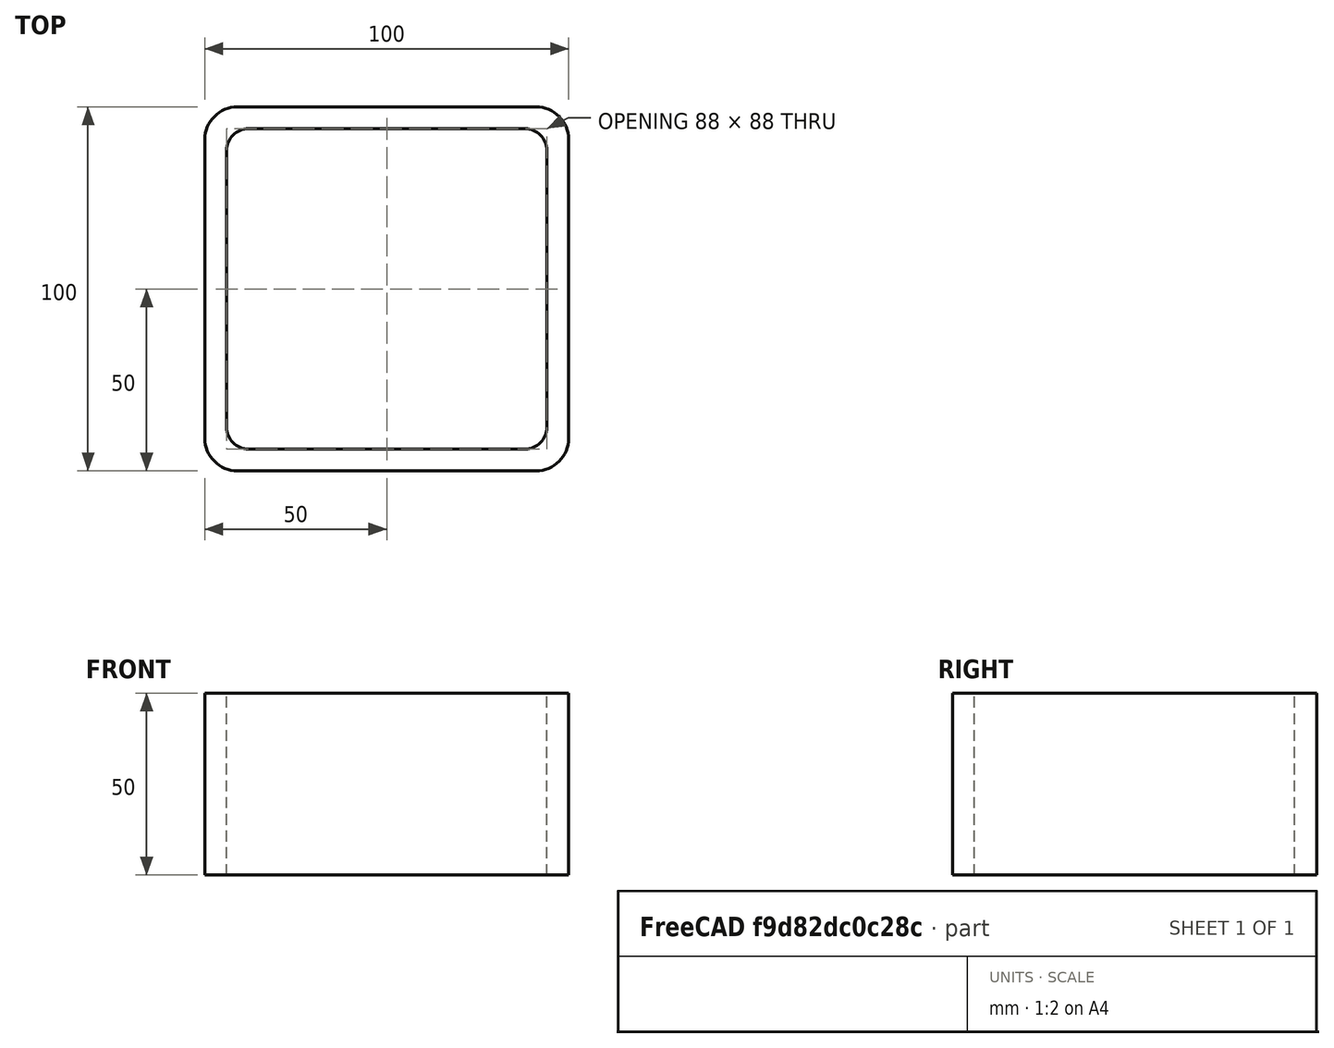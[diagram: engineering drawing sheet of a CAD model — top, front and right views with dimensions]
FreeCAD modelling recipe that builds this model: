
FCSTD DOCUMENT  (FreeCAD 0.15R4671 (Git))
Label: Square hollow section 100x100x6 EN10219 S235JRH
License: All rights reserved
LicenseURL: http://en.wikipedia.org/wiki/All_rights_reserved
objects: Sketcher::SketchObject×1, Part::Extrusion×1
note: 2 computed .brp shape members not serialized (recipe doc carries the construction recipe); baked Part::Feature solids carry a one-line shape summary decoded from their .brp

FEATURE [Sketcher::SketchObject] Sketch
  sketch-geometry (16):
    g0: LineSegment StartX=-38 StartY=44 StartZ=0 EndX=38 EndY=44 EndZ=0
    g1: LineSegment StartX=44 StartY=38 StartZ=0 EndX=44 EndY=-38 EndZ=0
    g2: LineSegment StartX=38 StartY=-44 StartZ=0 EndX=-38 EndY=-44 EndZ=0
    g3: LineSegment StartX=-44 StartY=-38 StartZ=0 EndX=-44 EndY=38 EndZ=0
    g4: LineSegment StartX=-41 StartY=50 StartZ=0 EndX=41 EndY=50 EndZ=0
    g5: LineSegment StartX=50 StartY=41 StartZ=0 EndX=50 EndY=-41 EndZ=0
    g6: LineSegment StartX=41 StartY=-50 StartZ=0 EndX=-41 EndY=-50 EndZ=0
    g7: LineSegment StartX=-50 StartY=-41 StartZ=0 EndX=-50 EndY=41 EndZ=0
    g8: ArcOfCircle CenterX=-38 CenterY=38 CenterZ=0 NormalX=0 NormalY=0 NormalZ=1 Radius=6 StartAngle=1.5708 EndAngle=3.14159
    g9: ArcOfCircle CenterX=38 CenterY=38 CenterZ=0 NormalX=0 NormalY=0 NormalZ=1 Radius=6 StartAngle=0 EndAngle=1.5708
    g10: ArcOfCircle CenterX=38 CenterY=-38 CenterZ=0 NormalX=0 NormalY=0 NormalZ=1 Radius=6 StartAngle=4.71239 EndAngle=6.28319
    g11: ArcOfCircle CenterX=-38 CenterY=-38 CenterZ=0 NormalX=0 NormalY=0 NormalZ=1 Radius=6 StartAngle=3.14159 EndAngle=4.71239
    g12: ArcOfCircle CenterX=41 CenterY=41 CenterZ=0 NormalX=0 NormalY=0 NormalZ=1 Radius=9 StartAngle=0 EndAngle=1.5708
    g13: ArcOfCircle CenterX=41 CenterY=-41 CenterZ=0 NormalX=0 NormalY=0 NormalZ=1 Radius=9 StartAngle=4.71239 EndAngle=6.28319
    g14: ArcOfCircle CenterX=-41 CenterY=-41 CenterZ=0 NormalX=0 NormalY=0 NormalZ=1 Radius=9 StartAngle=3.14159 EndAngle=4.71239
    g15: ArcOfCircle CenterX=-41 CenterY=41 CenterZ=0 NormalX=0 NormalY=0 NormalZ=1 Radius=9 StartAngle=1.5708 EndAngle=3.14159
  constraints (36):
    c: Horizontal(g2)
    c: Vertical(g3)
    c: Horizontal(g6)
    c: Vertical(g7)
    c: Tangent(g3,g8) = 1.5708
    c: Tangent(g0,g8) = 1.5708
    c: Tangent(g0,g9) = 1.5708
    c: Tangent(g1,g9) = 1.5708
    c: Tangent(g1,g10) = 1.5708
    c: Tangent(g2,g10) = 1.5708
    c: Tangent(g2,g11) = 1.5708
    c: Tangent(g3,g11) = 1.5708
    c: Tangent(g4,g12) = 1.5708
    c: Tangent(g5,g12) = 1.5708
    c: Tangent(g5,g13) = 1.5708
    c: Tangent(g6,g13) = 1.5708
    c: Tangent(g6,g14) = 1.5708
    c: Tangent(g7,g14) = 1.5708
    c: Tangent(g7,g15) = 1.5708
    c: Tangent(g4,g15) = 1.5708
    c: Equal(g9,g8)
    c: Equal(g9,g11)
    c: Equal(g9,g10)
    c: Equal(g12,g15)
    c: Equal(g12,g14)
    c: Equal(g12,g13)
    c: Symmetric(g4,g6,g-1)
    c: Symmetric(g7,g5,g-2)
    c: DistanceY(g4,g6) = -100
    c: DistanceX(g7,g5) = 100
    c: Symmetric(g3,g1,g-2)
    c: Symmetric(g0,g2,g-1)
    c: DistanceY(g0,g4) = 6
    c: DistanceX(g5,g1) = -6
    c: Radius(g9) = 6
    c: Radius(g12) = 9
FEATURE [Part::Extrusion] Extrude  label="Square hollow section 100x100x6 EN10219 S235JRH"
  Base = -> Sketch
  Dir = (0,0,50)
  Solid = true
